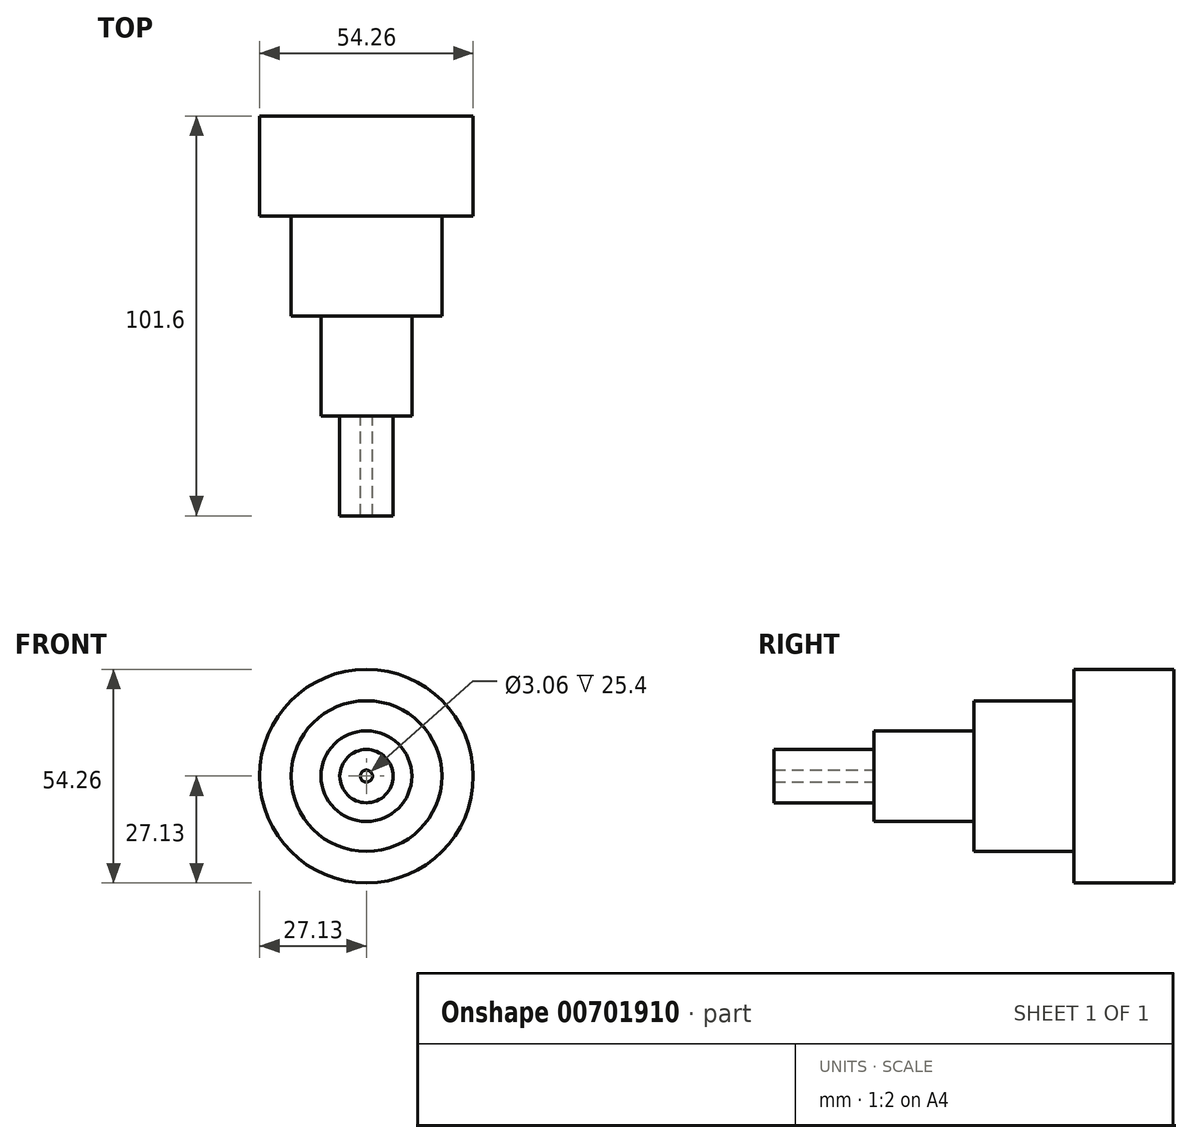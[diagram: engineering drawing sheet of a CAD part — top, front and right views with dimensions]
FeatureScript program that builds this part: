
annotation { "Feature Type Name" : "Feature", "Feature Type Description" : "" }
export const myFeature = defineFeature(function(context is Context, id is Id, definition is map)
    precondition{}
    {
        {
            var Q0;
            Q0=qCreatedBy(makeId("Front.planeOp"),FACE);
            var sketch = newSketch(context, id + "F0", { "sketchPlane" : qUnion([Q0])});
            skCircle(sketch, "E0", {"center": v(0, 0) * mm, "radius": 27.13 * mm});
            skSolve(sketch);
        }
        {
            var Q0;
            Q0=makeQuery(id+"F0.imprint","IMPRINT",FACE,{"disambiguationData":[TD([[makeQuery(id+"F0.imprint","IMPRINT",EDGE,{"derivedFrom":sQuery(id+"F0.wireOp",EDGE,"E0")}),1.0]])]});
            extrude(context, id + "F1", {"entities" : qUnion([Q0]), "depth" : 25.4 * mm, "offsetDistance" : 25.4 * mm});
        }
        {
            var Q0;
            Q0=makeQuery(id+"F1.opExtrude","CAP_FACE",FACE,{"disambiguationData":[OSD([sQuery(id+"F0.wireOp",EDGE,"E0")])],"isStart":false});
            var sketch = newSketch(context, id + "F2", { "sketchPlane" : qUnion([Q0])});
            skCircle(sketch, "E1", {"center": v(0, 0) * mm, "radius": 19.16 * mm});
            skSolve(sketch);
        }
        {
            var Q0;
            Q0 = qSketchRegion(id + "F2", true);
            extrude(context, id + "F3", {"entities" : qUnion([Q0]), "operationType" : NewBodyOperationType.ADD, "depth" : 25.4 * mm, "offsetDistance" : 25.4 * mm});
        }
        {
            var Q0;
            Q0=makeQuery(id+"F3.opExtrude","CAP_FACE",FACE,{"disambiguationData":[OSD([sQuery(id+"F2.wireOp",EDGE,"E1")])],"isStart":false});
            var sketch = newSketch(context, id + "F4", { "sketchPlane" : qUnion([Q0])});
            skCircle(sketch, "E2", {"center": v(0, 0) * mm, "radius": 11.53 * mm});
            skSolve(sketch);
        }
        {
            var Q0;
            Q0 = qSketchRegion(id + "F4", true);
            extrude(context, id + "F5", {"entities" : qUnion([Q0]), "operationType" : NewBodyOperationType.ADD, "depth" : 25.4 * mm, "offsetDistance" : 25.4 * mm});
        }
        {
            var Q0;
            Q0=makeQuery(id+"F5.opExtrude","CAP_FACE",FACE,{"disambiguationData":[OSD([sQuery(id+"F4.wireOp",EDGE,"E2")])],"isStart":false});
            var sketch = newSketch(context, id + "F6", { "sketchPlane" : qUnion([Q0])});
            skCircle(sketch, "E3", {"center": v(0, 0) * mm, "radius": 1.53 * mm});
            skCircle(sketch, "E4", {"center": v(0, 0) * mm, "radius": 6.77 * mm});
            skSolve(sketch);
        }
        {
            var Q0;
            Q0 = qSketchRegion(id + "F6", true);
            extrude(context, id + "F7", {"entities" : qUnion([Q0]), "operationType" : NewBodyOperationType.ADD, "depth" : 25.4 * mm, "offsetDistance" : 25.4 * mm});
        }
        {
            var Q0;
            Q0=makeQuery(id+"F7.opExtrude","CAP_FACE",FACE,{"disambiguationData":[OSD([sQuery(id+"F6.wireOp",EDGE,"E3"),sQuery(id+"F6.wireOp",EDGE,"E4")])],"isStart":false});
            var sketch = newSketch(context, id + "F8", { "sketchPlane" : qUnion([Q0])});
            skCircle(sketch, "E5", {"center": v(0, 0) * mm, "radius": 4.02 * mm});
            skSolve(sketch);
        }
        {
            var Q0;
            Q0=sQuery(id+"F8.wireOp",EDGE,"E5");
            extrude(context, id + "F9", {"bodyType" : ToolBodyType.SURFACE, "surfaceEntities" : qUnion([Q0]), "depth" : 25.4 * mm, "offsetDistance" : 25.4 * mm});
        }
    });
